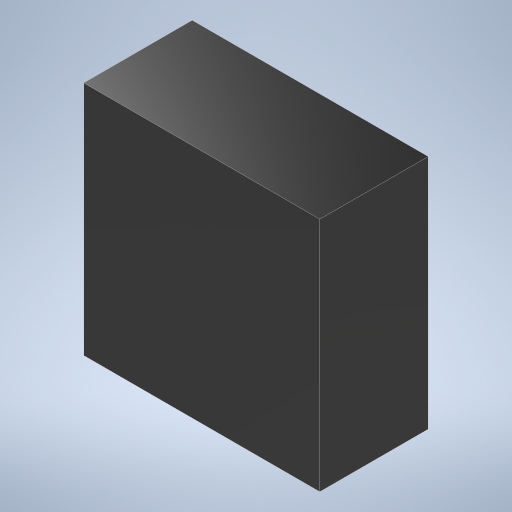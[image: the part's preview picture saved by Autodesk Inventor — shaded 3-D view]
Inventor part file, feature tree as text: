
AUTODESK INVENTOR PART (.ipt)
format: ipt  version: 2024 (Build 280153000, 153)  size: 184,320 bytes
history: native  units: mm
features: extrude x1, sketch x1
ambient origin geometry x8: Origin, YZ Plane, XZ Plane, XY Plane, X Axis, Y Axis, Z Axis, Center Point
bodies: Volumenkörper1 (feature_tree)
feature tree (2):
  extrude  "Extrusion1"  Depth=74.0mm
  sketch  "Skizze1"  dims[d0=74.0mm d1=74.0mm d2=34.0mm d3=0.0mm]
